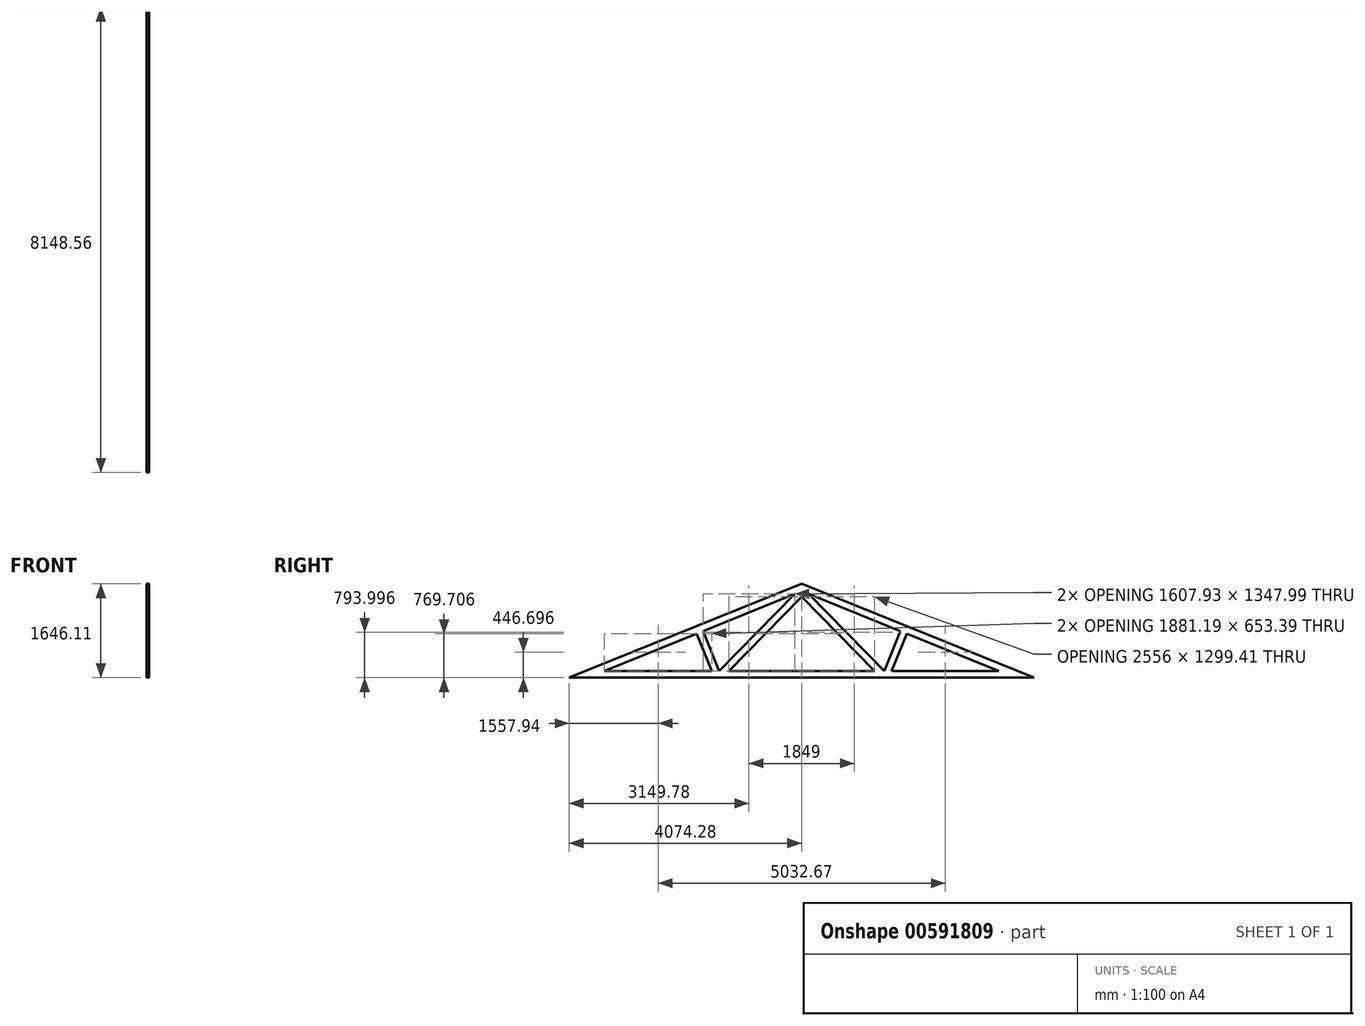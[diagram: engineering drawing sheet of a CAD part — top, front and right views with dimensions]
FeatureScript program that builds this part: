
annotation { "Feature Type Name" : "Feature", "Feature Type Description" : "" }
export const myFeature = defineFeature(function(context is Context, id is Id, definition is map)
    precondition{}
    {
        {
            var Q0;
            Q0=qCreatedBy(makeId("Right.planeOp"),FACE);
            var sketch = newSketch(context, id + "F0", { "sketchPlane" : qUnion([Q0]), "disableImprinting" : false});
            skLineSegment(sketch, "E0", {"start": v(-4100, 0) * mm, "end": v(4100, 0) * mm});
            skLineSegment(sketch, "E1", {"start": v(4100, 0) * mm, "end": v(0, 1656.5) * mm});
            skLineSegment(sketch, "E2", {"start": v(0, 1656.5) * mm, "end": v(-4100, 0) * mm});
            skLineSegment(sketch, "E3.0", {"start": v(0, 1651.11) * mm, "end": v(-4074.28, 5) * mm});
            skLineSegment(sketch, "E3.1", {"start": v(4074.28, 5) * mm, "end": v(0, 1651.11) * mm});
            skLineSegment(sketch, "E3.2", {"start": v(-4074.28, 5) * mm, "end": v(4074.28, 5) * mm});
            skLineSegment(sketch, "E4.0", {"start": v(-120.53, 1473) * mm, "end": v(-3456.93, 125) * mm});
            skLineSegment(sketch, "E4.1", {"start": v(3456.93, 125) * mm, "end": v(120.53, 1473) * mm});
            skLineSegment(sketch, "E4.2", {"start": v(-3456.93, 125) * mm, "end": v(-1575.74, 125) * mm});
            skLineSegment(sketch, "E5", {"start": v(-1728.47, 823.35) * mm, "end": v(-1446.32, 125) * mm});
            skLineSegment(sketch, "E6", {"start": v(1728.47, 823.35) * mm, "end": v(1446.32, 125) * mm});
            skLineSegment(sketch, "E7", {"start": v(-120.53, 1473) * mm, "end": v(-1446.32, 125) * mm});
            skLineSegment(sketch, "E8", {"start": v(120.53, 1473) * mm, "end": v(1446.32, 125) * mm});
            skLineSegment(sketch, "E9.0", {"start": v(1839.73, 778.4) * mm, "end": v(1575.74, 125) * mm});
            skLineSegment(sketch, "E10.0", {"start": v(-1839.73, 778.4) * mm, "end": v(-1575.74, 125) * mm});
            skLineSegment(sketch, "E11.0", {"start": v(-34.98, 1388.85) * mm, "end": v(-1278, 125) * mm});
            skLineSegment(sketch, "E12.0", {"start": v(34.98, 1388.85) * mm, "end": v(1278, 125) * mm});
            skLineSegment(sketch, "E13", {"start": v(34.98, 1388.85) * mm, "end": v(0, 1424.41) * mm});
            skLineSegment(sketch, "E14", {"start": v(-34.98, 1388.85) * mm, "end": v(0, 1424.41) * mm});
            skPoint(sketch, "E15.orphan", {"position": v(0, 1521.7) * mm});
            skLineSegment(sketch, "E16.trimOffspring", {"start": v(1575.74, 125) * mm, "end": v(3456.93, 125) * mm});
            skLineSegment(sketch, "E17.trimOffspring", {"start": v(-1278, 125) * mm, "end": v(1278, 125) * mm});
            skLineSegment(sketch, "E18", {"start": v(-1575.74, 125) * mm, "end": v(-1278, 125) * mm});
            skLineSegment(sketch, "E19", {"start": v(1575.74, 125) * mm, "end": v(1278, 125) * mm});
            skLineSegment(sketch, "E20", {"start": v(-120.53, 1473) * mm, "end": v(0, 1521.7) * mm});
            skLineSegment(sketch, "E21", {"start": v(120.53, 1473) * mm, "end": v(0, 1521.7) * mm});
            skLineSegment(sketch, "E22", {"start": v(0, 1424.41) * mm, "end": v(0, 1521.7) * mm});
            skSolve(sketch);
        }
        {
            var Q0;
            Q0=makeQuery(id+"F0.imprint","IMPRINT",FACE,{"disambiguationData":[TD([[makeQuery(id+"F0.imprint","IMPRINT",EDGE,{"derivedFrom":sQuery(id+"F0.wireOp",EDGE,"E3.0")}),1.0]])]});
            var Q1;
            {var subQ0=sQuery(id+"F0.wireOp",EDGE,"E5");Q1=makeQuery(id+"F0.imprint","IMPRINT",FACE,{"disambiguationData":[TD([[makeQuery(id+"F0.imprint","IMPRINT",EDGE,{"derivedFrom":subQ0}),-1.0]])]});}
            var Q2;
            {var subQ1=sQuery(id+"F0.wireOp",EDGE,"E7");Q2=makeQuery(id+"F0.imprint","IMPRINT",FACE,{"disambiguationData":[TD([[makeQuery(id+"F0.imprint","IMPRINT",EDGE,{"derivedFrom":subQ1}),1.0]])]});}
            var Q3;
            {var subQ1=sQuery(id+"F0.wireOp",EDGE,"E8");Q3=makeQuery(id+"F0.imprint","IMPRINT",FACE,{"disambiguationData":[TD([[makeQuery(id+"F0.imprint","IMPRINT",EDGE,{"derivedFrom":subQ1}),-1.0]])]});}
            var Q4;
            {var subQ0=sQuery(id+"F0.wireOp",EDGE,"E6");Q4=makeQuery(id+"F0.imprint","IMPRINT",FACE,{"disambiguationData":[TD([[makeQuery(id+"F0.imprint","IMPRINT",EDGE,{"derivedFrom":subQ0}),1.0]])]});}
            extrude(context, id + "F1", {"entities" : qUnion([Q0, Q1, Q2, Q3, Q4]), "depth" : 45 * mm, "offsetDistance" : 25 * mm});
        }
    });
